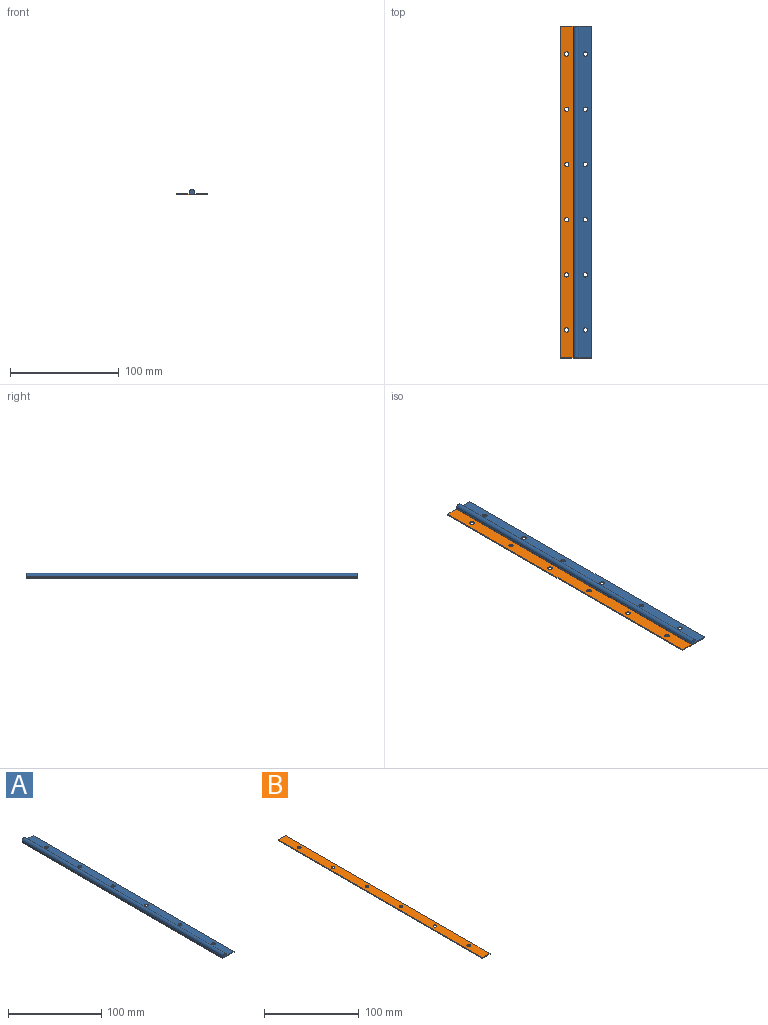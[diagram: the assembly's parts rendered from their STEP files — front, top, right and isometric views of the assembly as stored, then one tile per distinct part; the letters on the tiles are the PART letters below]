
ASSEMBLY  parts=2 mates=1
PART A: 14 faces, bbox 17x304.8x5 mm
  f0: plane 17x5mm, normal (0,-1,0), area 35.8mm2, adj f1,f9,f10,f11,f12,f13
  f1: plane 304.8x1mm, normal (1,0,0), area 304.8mm2, adj f0,f8,f9,f10
  f2: cylinder r=2mm len=4mm, axis (0,0,-1), area 12.6mm2, adj f9,f10
  f3: cylinder r=2mm len=4mm, axis (0,0,-1), area 12.6mm2, adj f9,f10
  f4: cylinder r=2mm len=4mm, axis (0,0,-1), area 12.6mm2, adj f9,f10
  f5: cylinder r=2mm len=4mm, axis (0,0,-1), area 12.6mm2, adj f9,f10
  f6: cylinder r=2mm len=4mm, axis (0,0,-1), area 12.6mm2, adj f9,f10
  f7: cylinder r=2mm len=4mm, axis (0,0,-1), area 12.6mm2, adj f9,f10
  f8: plane 17x5mm, normal (0,1,0), area 35.8mm2, adj f1,f9,f10,f11,f12,f13
  f9: plane 304.8x11.5mm, normal (0,0,1), area 3429.8mm2, adj f0,f1,f2,f3,f4,f5,f6,f7
  f10: plane 304.8x17mm, normal (0,0,-1), area 5106.2mm2, adj f0,f1,f2,f3,f4,f5,f6,f7
  f11: plane 304.8x1.25mm, normal (1,0,0), area 381mm2, adj f0,f8,f9,f13
  f12: plane 304.8x2.25mm, normal (-1,0,0), area 685.8mm2, adj f0,f8,f10,f13
  f13: cylinder r=2.75mm len=304.8mm, axis (0,1,0), area 2633.3mm2, adj f0,f8,f11,f12
PART B: 12 faces, bbox 11.5x304.8x1 mm
  f0: plane 11.5x1mm, normal (0,-1,0), area 11.5mm2, adj f1,f9,f10,f11
  f1: plane 304.8x1mm, normal (1,0,0), area 304.8mm2, adj f0,f2,f10,f11
  f2: plane 11.5x1mm, normal (0,1,0), area 11.5mm2, adj f1,f9,f10,f11
  f3: cylinder r=2mm len=4mm, axis (0,0,-1), area 12.6mm2, adj f10,f11
  f4: cylinder r=2mm len=4mm, axis (0,0,-1), area 12.6mm2, adj f10,f11
  f5: cylinder r=2mm len=4mm, axis (0,0,-1), area 12.6mm2, adj f10,f11
  f6: cylinder r=2mm len=4mm, axis (0,0,-1), area 12.6mm2, adj f10,f11
  f7: cylinder r=2mm len=4mm, axis (0,0,-1), area 12.6mm2, adj f10,f11
  f8: cylinder r=2mm len=4mm, axis (0,0,-1), area 12.6mm2, adj f10,f11
  f9: plane 304.8x1mm, normal (-1,0,0), area 304.8mm2, adj f0,f2,f10,f11
  f10: plane 304.8x11.5mm, normal (0,0,1), area 3429.8mm2, adj f0,f1,f2,f3,f4,f5,f6,f7
  f11: plane 304.8x11.5mm, normal (0,0,-1), area 3429.8mm2, adj f0,f1,f2,f3,f4,f5,f6,f7
PLACE A t=(17.37,-105.02,51.85)mm fixed
PLACE B t=(17.37,-105.02,51.85)mm
MATE revolute B.f0 <-> A.f0  axis (0,-1,0) through (17.37,-105.02,51.85)mm
